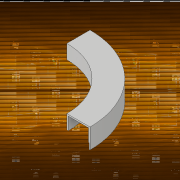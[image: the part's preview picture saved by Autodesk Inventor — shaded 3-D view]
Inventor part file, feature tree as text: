
AUTODESK INVENTOR PART (.ipt)
format: ipt  version: 2017 (Build 210142000, 142)  size: 168,448 bytes
history: native  units: in
note: dims shown in document units (in); Inventor stores cm internally (conversion verified against a paired STEP export)
features: sketch x2, revolve x1, extrude x1
ambient origin geometry x8: Origin, YZ Plane, XZ Plane, XY Plane, X Axis, Y Axis, Z Axis, Center Point
bodies: Solid1 (feature_tree)
feature tree (4):
  revolve  "Revolution1"  [1 undecoded]
  extrude  "Extrusion1"  Depth=2.875in
  sketch  "Sketch1"  dims[d0=2.0in d2=10.5in]
  sketch  "Sketch2"  dims[d3=2.0in d4=2.875in d5=0.125in d6=0.125in d7=0.125in d8=0.125in d9=0.125in d10=0.125in d11=0.125in d12=0.125in d13=1.0285in d14=0.5in d15=180.0deg d16=5.25in d17=0.125in d18=0.125in d19=0.25in d20=0.0625in d21=0.25in d22=0.25in d23=1.0in d24=0.0in]
note: 1 required parameter value undecoded (feature->parameter linkage not recoverable at this tier; creation-order binding heuristic only, values carry confidence <= 0.55)
